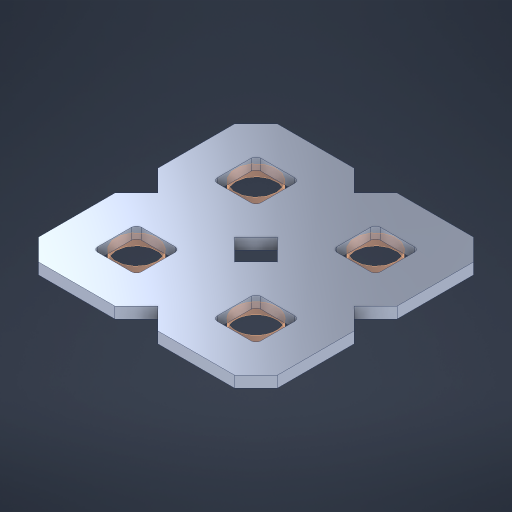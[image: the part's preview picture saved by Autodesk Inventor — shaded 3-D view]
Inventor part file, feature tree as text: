
AUTODESK INVENTOR PART (.ipt)
format: ipt  version: 2023 (Build 270158000, 158)  size: 285,696 bytes
history: native  units: in
note: dims shown in document units (in); Inventor stores cm internally (conversion verified against a paired STEP export)
features: other x5, extrude x3, sketch x2, pattern_linear x1
ambient origin geometry x8: Origin, YZ Plane, XZ Plane, XY Plane, X Axis, Y Axis, Z Axis, Center Point
bodies: Solid1 (feature_tree), Body (feature_tree)
feature tree (11):
  pattern_linear  "Rectangular Pattern1"  Spacing1=0.09in  [1 undecoded]
  sketch  "Sketch1"  dims[d1=0.5in]
  sketch  "Sketch2"  dims[d2=0.182in d3=0.09in d4=0.09in d5=0.09in d6=0.09in d7=0.09in d8=0.09in d9=0.09in d10=0.09in d11=0.02in d13=0.0in d14=0.172in d15=0.0625in d16=0.0in d19=0.5in d22=0.5in]
  other  "Srf1"
  other  "Srf126"
  other  "Srf268"
  other  "Srf269"
  other  "Circle"
  extrude  "ExtrusionSrf126"  Depth=0.09in
  extrude  "ExtrusionSrf268"  Depth=0.09in
  extrude  "ExtrusionSrf269"  Depth=0.09in
note: 1 required parameter value undecoded (feature->parameter linkage not recoverable at this tier; creation-order binding heuristic only, values carry confidence <= 0.55)
